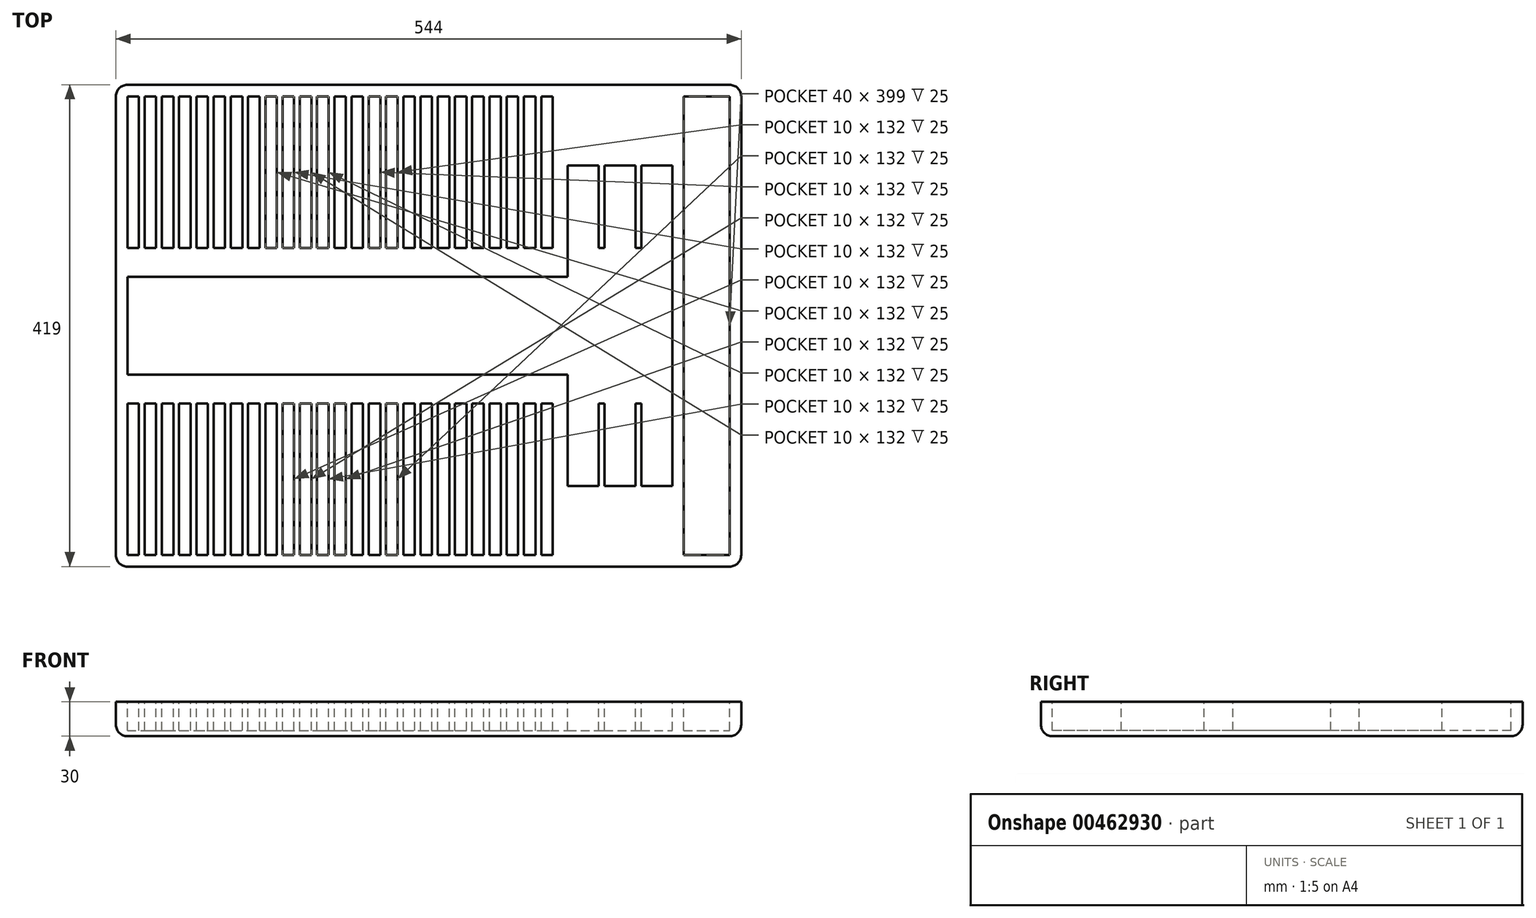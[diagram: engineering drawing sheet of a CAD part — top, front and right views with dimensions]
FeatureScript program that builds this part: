
annotation { "Feature Type Name" : "Feature", "Feature Type Description" : "" }
export const myFeature = defineFeature(function(context is Context, id is Id, definition is map)
    precondition{}
    {
        {
            var Q0;
            Q0=qCreatedBy(makeId("Top.planeOp"),FACE);
            var sketch = newSketch(context, id + "F0", { "sketchPlane" : qUnion([Q0])});
            skLineSegment(sketch, "E0.bottom", {"start": v(-272, -209.5) * mm, "end": v(272, -209.5) * mm});
            skLineSegment(sketch, "E0.top", {"start": v(-272, 209.5) * mm, "end": v(272, 209.5) * mm});
            skLineSegment(sketch, "E0.left", {"start": v(-272, -209.5) * mm, "end": v(-272, 209.5) * mm});
            skLineSegment(sketch, "E0.right", {"start": v(272, -209.5) * mm, "end": v(272, 209.5) * mm});
            skPoint(sketch, "E0.middle", {"position": v(0, 0) * mm});
            skSolve(sketch);
        }
        {
            var Q0;
            Q0 = qSketchRegion(id + "F0", true);
            extrude(context, id + "F1", {"entities" : qUnion([Q0]), "depth" : 30 * mm});
        }
        {
            var Q0;
            Q0=makeQuery(id+"F1.opExtrude","SWEPT_EDGE",EDGE,{"disambiguationData":[OSD([sQuery(id+"F0.wireOp",EDGE,"E0.bottom"),sQuery(id+"F0.wireOp",EDGE,"E0.left")])]});
            var Q1;
            Q1=makeQuery(id+"F1.opExtrude","SWEPT_EDGE",EDGE,{"disambiguationData":[OSD([sQuery(id+"F0.wireOp",EDGE,"E0.bottom"),sQuery(id+"F0.wireOp",EDGE,"E0.right")])]});
            var Q2;
            Q2=makeQuery(id+"F1.opExtrude","SWEPT_EDGE",EDGE,{"disambiguationData":[OSD([sQuery(id+"F0.wireOp",EDGE,"E0.top"),sQuery(id+"F0.wireOp",EDGE,"E0.right")])]});
            var Q3;
            Q3=makeQuery(id+"F1.opExtrude","SWEPT_EDGE",EDGE,{"disambiguationData":[OSD([sQuery(id+"F0.wireOp",EDGE,"E0.top"),sQuery(id+"F0.wireOp",EDGE,"E0.left")])]});
            fillet(context, id + "F2", {"entities" : qUnion([Q0, Q1, Q2, Q3]), "radius" : 10 * mm, "tangentPropagation" : true, "allowEdgeOverflow" : false});
        }
        {
            var Q0;
            Q0=makeQuery(id+"F1.opExtrude","CAP_EDGE",EDGE,{"disambiguationData":[OSD([sQuery(id+"F0.wireOp",EDGE,"E0.top")])],"isStart":true});
            fillet(context, id + "F3", {"entities" : qUnion([Q0]), "radius" : 10 * mm, "tangentPropagation" : true, "allowEdgeOverflow" : false});
        }
        {
            var Q0;
            Q0=makeQuery(id+"F1.opExtrude","CAP_FACE",FACE,{"disambiguationData":[OSD([sQuery(id+"F0.wireOp",EDGE,"E0.bottom"),sQuery(id+"F0.wireOp",EDGE,"E0.top"),sQuery(id+"F0.wireOp",EDGE,"E0.left"),sQuery(id+"F0.wireOp",EDGE,"E0.right")])],"isStart":false});
            var sketch = newSketch(context, id + "F4", { "sketchPlane" : qUnion([Q0])});
            skLineSegment(sketch, "E1.bottom", {"start": v(-262, -67.5) * mm, "end": v(-252, -67.5) * mm});
            skLineSegment(sketch, "E1.top", {"start": v(-262, -199.5) * mm, "end": v(-252, -199.5) * mm});
            skLineSegment(sketch, "E1.left", {"start": v(-262, -67.5) * mm, "end": v(-262, -199.5) * mm});
            skLineSegment(sketch, "E1.right", {"start": v(-252, -67.5) * mm, "end": v(-252, -199.5) * mm});
            skLineSegment(sketch, "E2.0.1.0", {"start": v(-262, 199.5) * mm, "end": v(-262, 67.5) * mm});
            skLineSegment(sketch, "E2.0.1.1", {"start": v(-252, 199.5) * mm, "end": v(-252, 67.5) * mm});
            skLineSegment(sketch, "E2.0.1.2", {"start": v(-262, 199.5) * mm, "end": v(-252, 199.5) * mm});
            skLineSegment(sketch, "E2.0.1.3", {"start": v(-262, 67.5) * mm, "end": v(-252, 67.5) * mm});
            skLineSegment(sketch, "E2.1.0.0", {"start": v(-247, -67.5) * mm, "end": v(-247, -199.5) * mm});
            skLineSegment(sketch, "E2.1.0.1", {"start": v(-237, -67.5) * mm, "end": v(-237, -199.5) * mm});
            skLineSegment(sketch, "E2.1.0.2", {"start": v(-247, -67.5) * mm, "end": v(-237, -67.5) * mm});
            skLineSegment(sketch, "E2.1.0.3", {"start": v(-247, -199.5) * mm, "end": v(-237, -199.5) * mm});
            skLineSegment(sketch, "E2.1.1.0", {"start": v(-247, 199.5) * mm, "end": v(-247, 67.5) * mm});
            skLineSegment(sketch, "E2.1.1.1", {"start": v(-237, 199.5) * mm, "end": v(-237, 67.5) * mm});
            skLineSegment(sketch, "E2.1.1.2", {"start": v(-247, 199.5) * mm, "end": v(-237, 199.5) * mm});
            skLineSegment(sketch, "E2.1.1.3", {"start": v(-247, 67.5) * mm, "end": v(-237, 67.5) * mm});
            skLineSegment(sketch, "E2.2.0.0", {"start": v(-232, -67.5) * mm, "end": v(-232, -199.5) * mm});
            skLineSegment(sketch, "E2.2.0.1", {"start": v(-222, -67.5) * mm, "end": v(-222, -199.5) * mm});
            skLineSegment(sketch, "E2.2.0.2", {"start": v(-232, -67.5) * mm, "end": v(-222, -67.5) * mm});
            skLineSegment(sketch, "E2.2.0.3", {"start": v(-232, -199.5) * mm, "end": v(-222, -199.5) * mm});
            skLineSegment(sketch, "E2.2.1.0", {"start": v(-232, 199.5) * mm, "end": v(-232, 67.5) * mm});
            skLineSegment(sketch, "E2.2.1.1", {"start": v(-222, 199.5) * mm, "end": v(-222, 67.5) * mm});
            skLineSegment(sketch, "E2.2.1.2", {"start": v(-232, 199.5) * mm, "end": v(-222, 199.5) * mm});
            skLineSegment(sketch, "E2.2.1.3", {"start": v(-232, 67.5) * mm, "end": v(-222, 67.5) * mm});
            skLineSegment(sketch, "E2.3.0.0", {"start": v(-217, -67.5) * mm, "end": v(-217, -199.5) * mm});
            skLineSegment(sketch, "E2.3.0.1", {"start": v(-207, -67.5) * mm, "end": v(-207, -199.5) * mm});
            skLineSegment(sketch, "E2.3.0.2", {"start": v(-217, -67.5) * mm, "end": v(-207, -67.5) * mm});
            skLineSegment(sketch, "E2.3.0.3", {"start": v(-217, -199.5) * mm, "end": v(-207, -199.5) * mm});
            skLineSegment(sketch, "E2.3.1.0", {"start": v(-217, 199.5) * mm, "end": v(-217, 67.5) * mm});
            skLineSegment(sketch, "E2.3.1.1", {"start": v(-207, 199.5) * mm, "end": v(-207, 67.5) * mm});
            skLineSegment(sketch, "E2.3.1.2", {"start": v(-217, 199.5) * mm, "end": v(-207, 199.5) * mm});
            skLineSegment(sketch, "E2.3.1.3", {"start": v(-217, 67.5) * mm, "end": v(-207, 67.5) * mm});
            skLineSegment(sketch, "E2.4.0.0", {"start": v(-202, -67.5) * mm, "end": v(-202, -199.5) * mm});
            skLineSegment(sketch, "E2.4.0.1", {"start": v(-192, -67.5) * mm, "end": v(-192, -199.5) * mm});
            skLineSegment(sketch, "E2.4.0.2", {"start": v(-202, -67.5) * mm, "end": v(-192, -67.5) * mm});
            skLineSegment(sketch, "E2.4.0.3", {"start": v(-202, -199.5) * mm, "end": v(-192, -199.5) * mm});
            skLineSegment(sketch, "E2.4.1.0", {"start": v(-202, 199.5) * mm, "end": v(-202, 67.5) * mm});
            skLineSegment(sketch, "E2.4.1.1", {"start": v(-192, 199.5) * mm, "end": v(-192, 67.5) * mm});
            skLineSegment(sketch, "E2.4.1.2", {"start": v(-202, 199.5) * mm, "end": v(-192, 199.5) * mm});
            skLineSegment(sketch, "E2.4.1.3", {"start": v(-202, 67.5) * mm, "end": v(-192, 67.5) * mm});
            skLineSegment(sketch, "E2.5.0.0", {"start": v(-187, -67.5) * mm, "end": v(-187, -199.5) * mm});
            skLineSegment(sketch, "E2.5.0.1", {"start": v(-177, -67.5) * mm, "end": v(-177, -199.5) * mm});
            skLineSegment(sketch, "E2.5.0.2", {"start": v(-187, -67.5) * mm, "end": v(-177, -67.5) * mm});
            skLineSegment(sketch, "E2.5.0.3", {"start": v(-187, -199.5) * mm, "end": v(-177, -199.5) * mm});
            skLineSegment(sketch, "E2.5.1.0", {"start": v(-187, 199.5) * mm, "end": v(-187, 67.5) * mm});
            skLineSegment(sketch, "E2.5.1.1", {"start": v(-177, 199.5) * mm, "end": v(-177, 67.5) * mm});
            skLineSegment(sketch, "E2.5.1.2", {"start": v(-187, 199.5) * mm, "end": v(-177, 199.5) * mm});
            skLineSegment(sketch, "E2.5.1.3", {"start": v(-187, 67.5) * mm, "end": v(-177, 67.5) * mm});
            skLineSegment(sketch, "E2.6.0.0", {"start": v(-172, -67.5) * mm, "end": v(-172, -199.5) * mm});
            skLineSegment(sketch, "E2.6.0.1", {"start": v(-162, -67.5) * mm, "end": v(-162, -199.5) * mm});
            skLineSegment(sketch, "E2.6.0.2", {"start": v(-172, -67.5) * mm, "end": v(-162, -67.5) * mm});
            skLineSegment(sketch, "E2.6.0.3", {"start": v(-172, -199.5) * mm, "end": v(-162, -199.5) * mm});
            skLineSegment(sketch, "E2.6.1.0", {"start": v(-172, 199.5) * mm, "end": v(-172, 67.5) * mm});
            skLineSegment(sketch, "E2.6.1.1", {"start": v(-162, 199.5) * mm, "end": v(-162, 67.5) * mm});
            skLineSegment(sketch, "E2.6.1.2", {"start": v(-172, 199.5) * mm, "end": v(-162, 199.5) * mm});
            skLineSegment(sketch, "E2.6.1.3", {"start": v(-172, 67.5) * mm, "end": v(-162, 67.5) * mm});
            skLineSegment(sketch, "E2.7.0.0", {"start": v(-157, -67.5) * mm, "end": v(-157, -199.5) * mm});
            skLineSegment(sketch, "E2.7.0.1", {"start": v(-147, -67.5) * mm, "end": v(-147, -199.5) * mm});
            skLineSegment(sketch, "E2.7.0.2", {"start": v(-157, -67.5) * mm, "end": v(-147, -67.5) * mm});
            skLineSegment(sketch, "E2.7.0.3", {"start": v(-157, -199.5) * mm, "end": v(-147, -199.5) * mm});
            skLineSegment(sketch, "E2.7.1.0", {"start": v(-157, 199.5) * mm, "end": v(-157, 67.5) * mm});
            skLineSegment(sketch, "E2.7.1.1", {"start": v(-147, 199.5) * mm, "end": v(-147, 67.5) * mm});
            skLineSegment(sketch, "E2.7.1.2", {"start": v(-157, 199.5) * mm, "end": v(-147, 199.5) * mm});
            skLineSegment(sketch, "E2.7.1.3", {"start": v(-157, 67.5) * mm, "end": v(-147, 67.5) * mm});
            skLineSegment(sketch, "E2.8.0.0", {"start": v(-142, -67.5) * mm, "end": v(-142, -199.5) * mm});
            skLineSegment(sketch, "E2.8.0.1", {"start": v(-132, -67.5) * mm, "end": v(-132, -199.5) * mm});
            skLineSegment(sketch, "E2.8.0.2", {"start": v(-142, -67.5) * mm, "end": v(-132, -67.5) * mm});
            skLineSegment(sketch, "E2.8.0.3", {"start": v(-142, -199.5) * mm, "end": v(-132, -199.5) * mm});
            skLineSegment(sketch, "E2.8.1.0", {"start": v(-142, 199.5) * mm, "end": v(-142, 67.5) * mm});
            skLineSegment(sketch, "E2.8.1.1", {"start": v(-132, 199.5) * mm, "end": v(-132, 67.5) * mm});
            skLineSegment(sketch, "E2.8.1.2", {"start": v(-142, 199.5) * mm, "end": v(-132, 199.5) * mm});
            skLineSegment(sketch, "E2.8.1.3", {"start": v(-142, 67.5) * mm, "end": v(-132, 67.5) * mm});
            skLineSegment(sketch, "E2.9.0.0", {"start": v(-127, -67.5) * mm, "end": v(-127, -199.5) * mm});
            skLineSegment(sketch, "E2.9.0.1", {"start": v(-117, -67.5) * mm, "end": v(-117, -199.5) * mm});
            skLineSegment(sketch, "E2.9.0.2", {"start": v(-127, -67.5) * mm, "end": v(-117, -67.5) * mm});
            skLineSegment(sketch, "E2.9.0.3", {"start": v(-127, -199.5) * mm, "end": v(-117, -199.5) * mm});
            skLineSegment(sketch, "E2.9.1.0", {"start": v(-127, 199.5) * mm, "end": v(-127, 67.5) * mm});
            skLineSegment(sketch, "E2.9.1.1", {"start": v(-117, 199.5) * mm, "end": v(-117, 67.5) * mm});
            skLineSegment(sketch, "E2.9.1.2", {"start": v(-127, 199.5) * mm, "end": v(-117, 199.5) * mm});
            skLineSegment(sketch, "E2.9.1.3", {"start": v(-127, 67.5) * mm, "end": v(-117, 67.5) * mm});
            skLineSegment(sketch, "E2.10.0.0", {"start": v(-112, -67.5) * mm, "end": v(-112, -199.5) * mm});
            skLineSegment(sketch, "E2.10.0.1", {"start": v(-102, -67.5) * mm, "end": v(-102, -199.5) * mm});
            skLineSegment(sketch, "E2.10.0.2", {"start": v(-112, -67.5) * mm, "end": v(-102, -67.5) * mm});
            skLineSegment(sketch, "E2.10.0.3", {"start": v(-112, -199.5) * mm, "end": v(-102, -199.5) * mm});
            skLineSegment(sketch, "E2.10.1.0", {"start": v(-112, 199.5) * mm, "end": v(-112, 67.5) * mm});
            skLineSegment(sketch, "E2.10.1.1", {"start": v(-102, 199.5) * mm, "end": v(-102, 67.5) * mm});
            skLineSegment(sketch, "E2.10.1.2", {"start": v(-112, 199.5) * mm, "end": v(-102, 199.5) * mm});
            skLineSegment(sketch, "E2.10.1.3", {"start": v(-112, 67.5) * mm, "end": v(-102, 67.5) * mm});
            skLineSegment(sketch, "E2.11.0.0", {"start": v(-97, -67.5) * mm, "end": v(-97, -199.5) * mm});
            skLineSegment(sketch, "E2.11.0.1", {"start": v(-87, -67.5) * mm, "end": v(-87, -199.5) * mm});
            skLineSegment(sketch, "E2.11.0.2", {"start": v(-97, -67.5) * mm, "end": v(-87, -67.5) * mm});
            skLineSegment(sketch, "E2.11.0.3", {"start": v(-97, -199.5) * mm, "end": v(-87, -199.5) * mm});
            skLineSegment(sketch, "E2.11.1.0", {"start": v(-97, 199.5) * mm, "end": v(-97, 67.5) * mm});
            skLineSegment(sketch, "E2.11.1.1", {"start": v(-87, 199.5) * mm, "end": v(-87, 67.5) * mm});
            skLineSegment(sketch, "E2.11.1.2", {"start": v(-97, 199.5) * mm, "end": v(-87, 199.5) * mm});
            skLineSegment(sketch, "E2.11.1.3", {"start": v(-97, 67.5) * mm, "end": v(-87, 67.5) * mm});
            skLineSegment(sketch, "E2.12.0.0", {"start": v(-82, -67.5) * mm, "end": v(-82, -199.5) * mm});
            skLineSegment(sketch, "E2.12.0.1", {"start": v(-72, -67.5) * mm, "end": v(-72, -199.5) * mm});
            skLineSegment(sketch, "E2.12.0.2", {"start": v(-82, -67.5) * mm, "end": v(-72, -67.5) * mm});
            skLineSegment(sketch, "E2.12.0.3", {"start": v(-82, -199.5) * mm, "end": v(-72, -199.5) * mm});
            skLineSegment(sketch, "E2.12.1.0", {"start": v(-82, 199.5) * mm, "end": v(-82, 67.5) * mm});
            skLineSegment(sketch, "E2.12.1.1", {"start": v(-72, 199.5) * mm, "end": v(-72, 67.5) * mm});
            skLineSegment(sketch, "E2.12.1.2", {"start": v(-82, 199.5) * mm, "end": v(-72, 199.5) * mm});
            skLineSegment(sketch, "E2.12.1.3", {"start": v(-82, 67.5) * mm, "end": v(-72, 67.5) * mm});
            skLineSegment(sketch, "E2.13.0.0", {"start": v(-67, -67.5) * mm, "end": v(-67, -199.5) * mm});
            skLineSegment(sketch, "E2.13.0.1", {"start": v(-57, -67.5) * mm, "end": v(-57, -199.5) * mm});
            skLineSegment(sketch, "E2.13.0.2", {"start": v(-67, -67.5) * mm, "end": v(-57, -67.5) * mm});
            skLineSegment(sketch, "E2.13.0.3", {"start": v(-67, -199.5) * mm, "end": v(-57, -199.5) * mm});
            skLineSegment(sketch, "E2.13.1.0", {"start": v(-67, 199.5) * mm, "end": v(-67, 67.5) * mm});
            skLineSegment(sketch, "E2.13.1.1", {"start": v(-57, 199.5) * mm, "end": v(-57, 67.5) * mm});
            skLineSegment(sketch, "E2.13.1.2", {"start": v(-67, 199.5) * mm, "end": v(-57, 199.5) * mm});
            skLineSegment(sketch, "E2.13.1.3", {"start": v(-67, 67.5) * mm, "end": v(-57, 67.5) * mm});
            skLineSegment(sketch, "E2.14.0.0", {"start": v(-52, -67.5) * mm, "end": v(-52, -199.5) * mm});
            skLineSegment(sketch, "E2.14.0.1", {"start": v(-42, -67.5) * mm, "end": v(-42, -199.5) * mm});
            skLineSegment(sketch, "E2.14.0.2", {"start": v(-52, -67.5) * mm, "end": v(-42, -67.5) * mm});
            skLineSegment(sketch, "E2.14.0.3", {"start": v(-52, -199.5) * mm, "end": v(-42, -199.5) * mm});
            skLineSegment(sketch, "E2.14.1.0", {"start": v(-52, 199.5) * mm, "end": v(-52, 67.5) * mm});
            skLineSegment(sketch, "E2.14.1.1", {"start": v(-42, 199.5) * mm, "end": v(-42, 67.5) * mm});
            skLineSegment(sketch, "E2.14.1.2", {"start": v(-52, 199.5) * mm, "end": v(-42, 199.5) * mm});
            skLineSegment(sketch, "E2.14.1.3", {"start": v(-52, 67.5) * mm, "end": v(-42, 67.5) * mm});
            skLineSegment(sketch, "E2.15.0.0", {"start": v(-37, -67.5) * mm, "end": v(-37, -199.5) * mm});
            skLineSegment(sketch, "E2.15.0.1", {"start": v(-27, -67.5) * mm, "end": v(-27, -199.5) * mm});
            skLineSegment(sketch, "E2.15.0.2", {"start": v(-37, -67.5) * mm, "end": v(-27, -67.5) * mm});
            skLineSegment(sketch, "E2.15.0.3", {"start": v(-37, -199.5) * mm, "end": v(-27, -199.5) * mm});
            skLineSegment(sketch, "E2.15.1.0", {"start": v(-37, 199.5) * mm, "end": v(-37, 67.5) * mm});
            skLineSegment(sketch, "E2.15.1.1", {"start": v(-27, 199.5) * mm, "end": v(-27, 67.5) * mm});
            skLineSegment(sketch, "E2.15.1.2", {"start": v(-37, 199.5) * mm, "end": v(-27, 199.5) * mm});
            skLineSegment(sketch, "E2.15.1.3", {"start": v(-37, 67.5) * mm, "end": v(-27, 67.5) * mm});
            skLineSegment(sketch, "E2.16.0.0", {"start": v(-22, -67.5) * mm, "end": v(-22, -199.5) * mm});
            skLineSegment(sketch, "E2.16.0.1", {"start": v(-12, -67.5) * mm, "end": v(-12, -199.5) * mm});
            skLineSegment(sketch, "E2.16.0.2", {"start": v(-22, -67.5) * mm, "end": v(-12, -67.5) * mm});
            skLineSegment(sketch, "E2.16.0.3", {"start": v(-22, -199.5) * mm, "end": v(-12, -199.5) * mm});
            skLineSegment(sketch, "E2.16.1.0", {"start": v(-22, 199.5) * mm, "end": v(-22, 67.5) * mm});
            skLineSegment(sketch, "E2.16.1.1", {"start": v(-12, 199.5) * mm, "end": v(-12, 67.5) * mm});
            skLineSegment(sketch, "E2.16.1.2", {"start": v(-22, 199.5) * mm, "end": v(-12, 199.5) * mm});
            skLineSegment(sketch, "E2.16.1.3", {"start": v(-22, 67.5) * mm, "end": v(-12, 67.5) * mm});
            skLineSegment(sketch, "E2.17.0.0", {"start": v(-7, -67.5) * mm, "end": v(-7, -199.5) * mm});
            skLineSegment(sketch, "E2.17.0.1", {"start": v(3, -67.5) * mm, "end": v(3, -199.5) * mm});
            skLineSegment(sketch, "E2.17.0.2", {"start": v(-7, -67.5) * mm, "end": v(3, -67.5) * mm});
            skLineSegment(sketch, "E2.17.0.3", {"start": v(-7, -199.5) * mm, "end": v(3, -199.5) * mm});
            skLineSegment(sketch, "E2.17.1.0", {"start": v(-7, 199.5) * mm, "end": v(-7, 67.5) * mm});
            skLineSegment(sketch, "E2.17.1.1", {"start": v(3, 199.5) * mm, "end": v(3, 67.5) * mm});
            skLineSegment(sketch, "E2.17.1.2", {"start": v(-7, 199.5) * mm, "end": v(3, 199.5) * mm});
            skLineSegment(sketch, "E2.17.1.3", {"start": v(-7, 67.5) * mm, "end": v(3, 67.5) * mm});
            skLineSegment(sketch, "E2.18.0.0", {"start": v(8, -67.5) * mm, "end": v(8, -199.5) * mm});
            skLineSegment(sketch, "E2.18.0.1", {"start": v(18, -67.5) * mm, "end": v(18, -199.5) * mm});
            skLineSegment(sketch, "E2.18.0.2", {"start": v(8, -67.5) * mm, "end": v(18, -67.5) * mm});
            skLineSegment(sketch, "E2.18.0.3", {"start": v(8, -199.5) * mm, "end": v(18, -199.5) * mm});
            skLineSegment(sketch, "E2.18.1.0", {"start": v(8, 199.5) * mm, "end": v(8, 67.5) * mm});
            skLineSegment(sketch, "E2.18.1.1", {"start": v(18, 199.5) * mm, "end": v(18, 67.5) * mm});
            skLineSegment(sketch, "E2.18.1.2", {"start": v(8, 199.5) * mm, "end": v(18, 199.5) * mm});
            skLineSegment(sketch, "E2.18.1.3", {"start": v(8, 67.5) * mm, "end": v(18, 67.5) * mm});
            skLineSegment(sketch, "E2.19.0.0", {"start": v(23, -67.5) * mm, "end": v(23, -199.5) * mm});
            skLineSegment(sketch, "E2.19.0.1", {"start": v(33, -67.5) * mm, "end": v(33, -199.5) * mm});
            skLineSegment(sketch, "E2.19.0.2", {"start": v(23, -67.5) * mm, "end": v(33, -67.5) * mm});
            skLineSegment(sketch, "E2.19.0.3", {"start": v(23, -199.5) * mm, "end": v(33, -199.5) * mm});
            skLineSegment(sketch, "E2.19.1.0", {"start": v(23, 199.5) * mm, "end": v(23, 67.5) * mm});
            skLineSegment(sketch, "E2.19.1.1", {"start": v(33, 199.5) * mm, "end": v(33, 67.5) * mm});
            skLineSegment(sketch, "E2.19.1.2", {"start": v(23, 199.5) * mm, "end": v(33, 199.5) * mm});
            skLineSegment(sketch, "E2.19.1.3", {"start": v(23, 67.5) * mm, "end": v(33, 67.5) * mm});
            skLineSegment(sketch, "E2.20.0.0", {"start": v(38, -67.5) * mm, "end": v(38, -199.5) * mm});
            skLineSegment(sketch, "E2.20.0.1", {"start": v(48, -67.5) * mm, "end": v(48, -199.5) * mm});
            skLineSegment(sketch, "E2.20.0.2", {"start": v(38, -67.5) * mm, "end": v(48, -67.5) * mm});
            skLineSegment(sketch, "E2.20.0.3", {"start": v(38, -199.5) * mm, "end": v(48, -199.5) * mm});
            skLineSegment(sketch, "E2.20.1.0", {"start": v(38, 199.5) * mm, "end": v(38, 67.5) * mm});
            skLineSegment(sketch, "E2.20.1.1", {"start": v(48, 199.5) * mm, "end": v(48, 67.5) * mm});
            skLineSegment(sketch, "E2.20.1.2", {"start": v(38, 199.5) * mm, "end": v(48, 199.5) * mm});
            skLineSegment(sketch, "E2.20.1.3", {"start": v(38, 67.5) * mm, "end": v(48, 67.5) * mm});
            skLineSegment(sketch, "E2.21.0.0", {"start": v(53, -67.5) * mm, "end": v(53, -199.5) * mm});
            skLineSegment(sketch, "E2.21.0.1", {"start": v(63, -67.5) * mm, "end": v(63, -199.5) * mm});
            skLineSegment(sketch, "E2.21.0.2", {"start": v(53, -67.5) * mm, "end": v(63, -67.5) * mm});
            skLineSegment(sketch, "E2.21.0.3", {"start": v(53, -199.5) * mm, "end": v(63, -199.5) * mm});
            skLineSegment(sketch, "E2.21.1.0", {"start": v(53, 199.5) * mm, "end": v(53, 67.5) * mm});
            skLineSegment(sketch, "E2.21.1.1", {"start": v(63, 199.5) * mm, "end": v(63, 67.5) * mm});
            skLineSegment(sketch, "E2.21.1.2", {"start": v(53, 199.5) * mm, "end": v(63, 199.5) * mm});
            skLineSegment(sketch, "E2.21.1.3", {"start": v(53, 67.5) * mm, "end": v(63, 67.5) * mm});
            skLineSegment(sketch, "E2.22.0.0", {"start": v(68, -67.5) * mm, "end": v(68, -199.5) * mm});
            skLineSegment(sketch, "E2.22.0.1", {"start": v(78, -67.5) * mm, "end": v(78, -199.5) * mm});
            skLineSegment(sketch, "E2.22.0.2", {"start": v(68, -67.5) * mm, "end": v(78, -67.5) * mm});
            skLineSegment(sketch, "E2.22.0.3", {"start": v(68, -199.5) * mm, "end": v(78, -199.5) * mm});
            skLineSegment(sketch, "E2.22.1.0", {"start": v(68, 199.5) * mm, "end": v(68, 67.5) * mm});
            skLineSegment(sketch, "E2.22.1.1", {"start": v(78, 199.5) * mm, "end": v(78, 67.5) * mm});
            skLineSegment(sketch, "E2.22.1.2", {"start": v(68, 199.5) * mm, "end": v(78, 199.5) * mm});
            skLineSegment(sketch, "E2.22.1.3", {"start": v(68, 67.5) * mm, "end": v(78, 67.5) * mm});
            skLineSegment(sketch, "E2.23.0.0", {"start": v(83, -67.5) * mm, "end": v(83, -199.5) * mm});
            skLineSegment(sketch, "E2.23.0.1", {"start": v(93, -67.5) * mm, "end": v(93, -199.5) * mm});
            skLineSegment(sketch, "E2.23.0.2", {"start": v(83, -67.5) * mm, "end": v(93, -67.5) * mm});
            skLineSegment(sketch, "E2.23.0.3", {"start": v(83, -199.5) * mm, "end": v(93, -199.5) * mm});
            skLineSegment(sketch, "E2.23.1.0", {"start": v(83, 199.5) * mm, "end": v(83, 67.5) * mm});
            skLineSegment(sketch, "E2.23.1.1", {"start": v(93, 199.5) * mm, "end": v(93, 67.5) * mm});
            skLineSegment(sketch, "E2.23.1.2", {"start": v(83, 199.5) * mm, "end": v(93, 199.5) * mm});
            skLineSegment(sketch, "E2.23.1.3", {"start": v(83, 67.5) * mm, "end": v(93, 67.5) * mm});
            skLineSegment(sketch, "E2.24.0.0", {"start": v(98, -67.5) * mm, "end": v(98, -199.5) * mm});
            skLineSegment(sketch, "E2.24.0.1", {"start": v(108, -67.5) * mm, "end": v(108, -199.5) * mm});
            skLineSegment(sketch, "E2.24.0.2", {"start": v(98, -67.5) * mm, "end": v(108, -67.5) * mm});
            skLineSegment(sketch, "E2.24.0.3", {"start": v(98, -199.5) * mm, "end": v(108, -199.5) * mm});
            skLineSegment(sketch, "E2.24.1.0", {"start": v(98, 199.5) * mm, "end": v(98, 67.5) * mm});
            skLineSegment(sketch, "E2.24.1.1", {"start": v(108, 199.5) * mm, "end": v(108, 67.5) * mm});
            skLineSegment(sketch, "E2.24.1.2", {"start": v(98, 199.5) * mm, "end": v(108, 199.5) * mm});
            skLineSegment(sketch, "E2.24.1.3", {"start": v(98, 67.5) * mm, "end": v(108, 67.5) * mm});
            skLineSegment(sketch, "E2.direction1", {"start": v(-262, -199.5) * mm, "end": v(-247, -199.5) * mm, "construction": true});
            skLineSegment(sketch, "E2.direction2", {"start": v(-262, -199.5) * mm, "end": v(-262, 67.5) * mm, "construction": true});
            skSolve(sketch);
        }
        {
            var Q0;
            Q0=makeQuery(id+"F1.opExtrude","CAP_FACE",FACE,{"disambiguationData":[OSD([sQuery(id+"F0.wireOp",EDGE,"E0.bottom"),sQuery(id+"F0.wireOp",EDGE,"E0.top"),sQuery(id+"F0.wireOp",EDGE,"E0.left"),sQuery(id+"F0.wireOp",EDGE,"E0.right")])],"isStart":false});
            var sketch = newSketch(context, id + "F5", { "sketchPlane" : qUnion([Q0])});
            skLineSegment(sketch, "E3.bottom", {"start": v(222, 199.5) * mm, "end": v(262, 199.5) * mm});
            skLineSegment(sketch, "E3.top", {"start": v(222, -199.5) * mm, "end": v(262, -199.5) * mm});
            skLineSegment(sketch, "E3.left", {"start": v(222, 199.5) * mm, "end": v(222, -199.5) * mm});
            skLineSegment(sketch, "E3.right", {"start": v(262, 199.5) * mm, "end": v(262, -199.5) * mm});
            skSolve(sketch);
        }
        {
            var Q0;
            Q0 = qSketchRegion(id + "F5", true);
            extrude(context, id + "F6", {"entities" : qUnion([Q0]), "operationType" : NewBodyOperationType.REMOVE, "oppositeDirection" : true, "depth" : 25 * mm});
        }
        {
            var Q0;
            Q0=makeQuery(id+"F1.opExtrude","CAP_FACE",FACE,{"disambiguationData":[OSD([sQuery(id+"F0.wireOp",EDGE,"E0.bottom"),sQuery(id+"F0.wireOp",EDGE,"E0.top"),sQuery(id+"F0.wireOp",EDGE,"E0.left"),sQuery(id+"F0.wireOp",EDGE,"E0.right")])],"isStart":false});
            var sketch = newSketch(context, id + "F7", { "sketchPlane" : qUnion([Q0])});
            skLineSegment(sketch, "E4.bottom", {"start": v(185, -67.5) * mm, "end": v(212, -67.5) * mm});
            skLineSegment(sketch, "E4.top", {"start": v(185, -139.5) * mm, "end": v(212, -139.5) * mm});
            skLineSegment(sketch, "E4.left", {"start": v(185, -67.5) * mm, "end": v(185, -139.5) * mm});
            skLineSegment(sketch, "E4.right", {"start": v(212, -67.5) * mm, "end": v(212, -139.5) * mm});
            skLineSegment(sketch, "E5.0.1.0", {"start": v(185, 67.5) * mm, "end": v(212, 67.5) * mm});
            skLineSegment(sketch, "E5.0.1.1", {"start": v(185, 139.5) * mm, "end": v(185, 67.5) * mm});
            skLineSegment(sketch, "E5.0.1.2", {"start": v(185, 139.5) * mm, "end": v(212, 139.5) * mm});
            skLineSegment(sketch, "E5.0.1.3", {"start": v(212, 139.5) * mm, "end": v(212, 67.5) * mm});
            skLineSegment(sketch, "E5.1.0.0", {"start": v(153, -139.5) * mm, "end": v(180, -139.5) * mm});
            skLineSegment(sketch, "E5.1.0.1", {"start": v(153, -67.5) * mm, "end": v(153, -139.5) * mm});
            skLineSegment(sketch, "E5.1.0.2", {"start": v(153, -67.5) * mm, "end": v(180, -67.5) * mm});
            skLineSegment(sketch, "E5.1.0.3", {"start": v(180, -67.5) * mm, "end": v(180, -139.5) * mm});
            skLineSegment(sketch, "E5.1.1.0", {"start": v(153, 67.5) * mm, "end": v(180, 67.5) * mm});
            skLineSegment(sketch, "E5.1.1.1", {"start": v(153, 139.5) * mm, "end": v(153, 67.5) * mm});
            skLineSegment(sketch, "E5.1.1.2", {"start": v(153, 139.5) * mm, "end": v(180, 139.5) * mm});
            skLineSegment(sketch, "E5.1.1.3", {"start": v(180, 139.5) * mm, "end": v(180, 67.5) * mm});
            skLineSegment(sketch, "E5.2.0.0", {"start": v(121, -139.5) * mm, "end": v(148, -139.5) * mm});
            skLineSegment(sketch, "E5.2.0.1", {"start": v(121, -67.5) * mm, "end": v(121, -139.5) * mm});
            skLineSegment(sketch, "E5.2.0.2", {"start": v(121, -67.5) * mm, "end": v(148, -67.5) * mm});
            skLineSegment(sketch, "E5.2.0.3", {"start": v(148, -67.5) * mm, "end": v(148, -139.5) * mm});
            skLineSegment(sketch, "E5.2.1.0", {"start": v(121, 67.5) * mm, "end": v(148, 67.5) * mm});
            skLineSegment(sketch, "E5.2.1.1", {"start": v(121, 139.5) * mm, "end": v(121, 67.5) * mm});
            skLineSegment(sketch, "E5.2.1.2", {"start": v(121, 139.5) * mm, "end": v(148, 139.5) * mm});
            skLineSegment(sketch, "E5.2.1.3", {"start": v(148, 139.5) * mm, "end": v(148, 67.5) * mm});
            skLineSegment(sketch, "E5.direction1", {"start": v(185, -139.5) * mm, "end": v(153, -139.5) * mm, "construction": true});
            skLineSegment(sketch, "E5.direction2", {"start": v(185, -139.5) * mm, "end": v(185, 67.5) * mm, "construction": true});
            skSolve(sketch);
        }
        {
            var Q0;
            Q0 = qSketchRegion(id + "F7", true);
            extrude(context, id + "F8", {"entities" : qUnion([Q0]), "operationType" : NewBodyOperationType.REMOVE, "oppositeDirection" : true, "depth" : 25 * mm});
        }
        {
            var Q0;
            Q0 = qSketchRegion(id + "F4", true);
            extrude(context, id + "F9", {"entities" : qUnion([Q0]), "operationType" : NewBodyOperationType.REMOVE, "oppositeDirection" : true, "depth" : 25 * mm});
        }
        {
            var Q0;
            Q0=makeQuery(id+"F1.opExtrude","CAP_FACE",FACE,{"disambiguationData":[OSD([sQuery(id+"F0.wireOp",EDGE,"E0.bottom"),sQuery(id+"F0.wireOp",EDGE,"E0.top"),sQuery(id+"F0.wireOp",EDGE,"E0.left"),sQuery(id+"F0.wireOp",EDGE,"E0.right")])],"isStart":false});
            var sketch = newSketch(context, id + "F10", { "sketchPlane" : qUnion([Q0])});
            skLineSegment(sketch, "E6.bottom", {"start": v(121, 67.5) * mm, "end": v(212, 67.5) * mm});
            skLineSegment(sketch, "E6.top", {"start": v(121, -67.5) * mm, "end": v(212, -67.5) * mm});
            skLineSegment(sketch, "E6.left", {"start": v(121, 67.5) * mm, "end": v(121, -67.5) * mm});
            skLineSegment(sketch, "E6.right", {"start": v(212, 67.5) * mm, "end": v(212, -67.5) * mm});
            skSolve(sketch);
        }
        {
            var Q0;
            Q0 = qSketchRegion(id + "F10", true);
            extrude(context, id + "F11", {"entities" : qUnion([Q0]), "operationType" : NewBodyOperationType.REMOVE, "oppositeDirection" : true, "depth" : 25 * mm});
        }
        {
            var Q0;
            Q0=makeQuery(id+"F1.opExtrude","CAP_FACE",FACE,{"disambiguationData":[OSD([sQuery(id+"F0.wireOp",EDGE,"E0.bottom"),sQuery(id+"F0.wireOp",EDGE,"E0.top"),sQuery(id+"F0.wireOp",EDGE,"E0.left"),sQuery(id+"F0.wireOp",EDGE,"E0.right")])],"isStart":false});
            var sketch = newSketch(context, id + "F12", { "sketchPlane" : qUnion([Q0])});
            skLineSegment(sketch, "E7.bottom", {"start": v(-262, 42.5) * mm, "end": v(121, 42.5) * mm});
            skLineSegment(sketch, "E7.top", {"start": v(-262, -42.5) * mm, "end": v(121, -42.5) * mm});
            skLineSegment(sketch, "E7.left", {"start": v(-262, 42.5) * mm, "end": v(-262, -42.5) * mm});
            skLineSegment(sketch, "E7.right", {"start": v(121, 42.5) * mm, "end": v(121, -42.5) * mm});
            skSolve(sketch);
        }
        {
            var Q0;
            Q0 = qSketchRegion(id + "F12", true);
            extrude(context, id + "F13", {"entities" : qUnion([Q0]), "operationType" : NewBodyOperationType.REMOVE, "oppositeDirection" : true, "depth" : 25 * mm});
        }
    });
